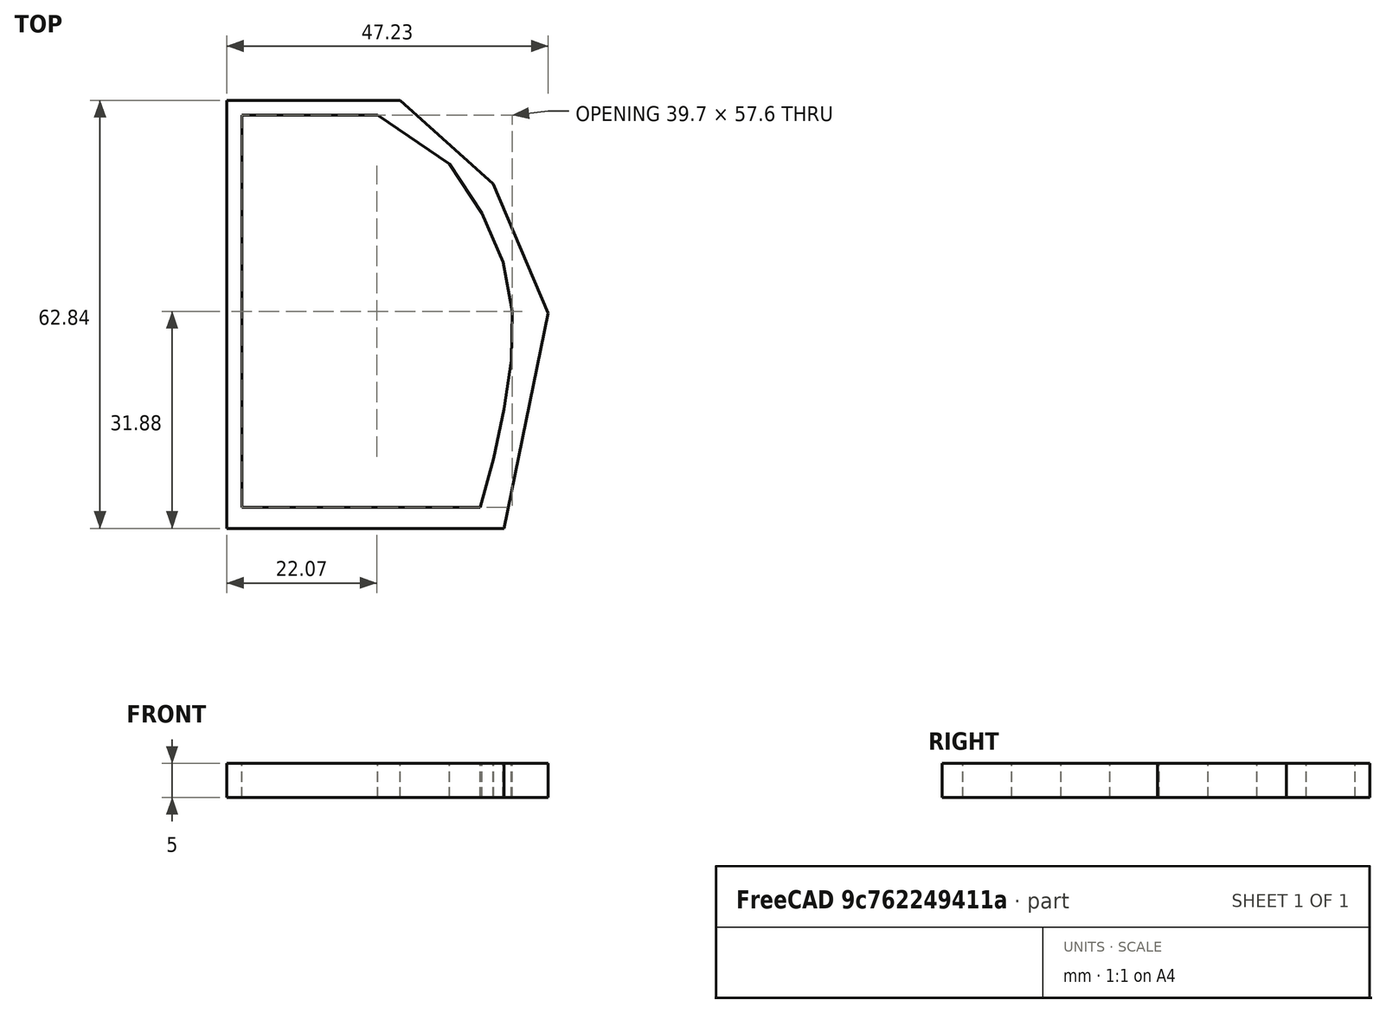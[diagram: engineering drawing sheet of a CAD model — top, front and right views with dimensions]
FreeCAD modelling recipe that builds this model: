
FCSTD DOCUMENT  (FreeCAD 0.19R24291 (Git))
Label: test-fob-profile
License: All rights reserved
LicenseURL: http://en.wikipedia.org/wiki/All_rights_reserved
objects: Sketcher::SketchObject×1, PartDesign::Pad×1, PartDesign::Body×1
note: 4 computed .brp shape members not serialized (recipe doc carries the construction recipe); baked Part::Feature solids carry a one-line shape summary decoded from their .brp

FEATURE [Sketcher::SketchObject] Sketch
  FullyConstrained = false
  MapMode = 5
  Support = -> [XY_Plane]
  sketch-geometry (17):
    g0: LineSegment StartX=0 StartY=0 StartZ=0 EndX=35 EndY=0 EndZ=0
    g1: LineSegment StartX=35 StartY=0 StartZ=0 EndX=37 EndY=7.2 EndZ=0
    g2: LineSegment StartX=37 StartY=7.2 StartZ=0 EndX=38.5 EndY=14.4 EndZ=0
    g3: LineSegment StartX=38.5 StartY=14.4 StartZ=0 EndX=39.6 EndY=21.6 EndZ=0
    g4: LineSegment StartX=39.6 StartY=21.6 StartZ=0 EndX=39.7 EndY=28.8 EndZ=0
    g5: LineSegment StartX=39.7 StartY=28.8 StartZ=0 EndX=38.4 EndY=36 EndZ=0
    g6: LineSegment StartX=38.4 StartY=36 StartZ=0 EndX=35.3 EndY=43.2 EndZ=0
    g7: LineSegment StartX=35.3 StartY=43.2 StartZ=0 EndX=30.5 EndY=50.4 EndZ=0
    g8: LineSegment StartX=30.5 StartY=50.4 StartZ=0 EndX=20 EndY=57.6 EndZ=0
    g9: LineSegment StartX=20 StartY=57.6 StartZ=0 EndX=0 EndY=57.6 EndZ=0
    g10: LineSegment StartX=0 StartY=57.6 StartZ=0 EndX=0 EndY=0 EndZ=0
    g11: LineSegment StartX=-2.21516 StartY=59.7598 StartZ=0 EndX=-2.21516 EndY=-3.07541 EndZ=0
    g12: LineSegment StartX=-2.21516 StartY=-3.07541 StartZ=0 EndX=38.4894 EndY=-3.07541 EndZ=0
    g13: LineSegment StartX=38.4894 StartY=-3.07541 StartZ=0 EndX=45.01 EndY=28.5398 EndZ=0
    g14: LineSegment StartX=45.01 StartY=28.5398 StartZ=0 EndX=36.9087 EndY=47.5089 EndZ=0
    g15: LineSegment StartX=36.9087 StartY=47.5089 StartZ=0 EndX=23.2746 EndY=59.7598 EndZ=0
    g16: LineSegment StartX=23.2746 StartY=59.7598 StartZ=0 EndX=-2.21516 EndY=59.7598 EndZ=0
  constraints (41):
    c: Coincident(g-1,g0)
    c: PointOnObject(g0,g-1)
    c: Coincident(g0,g1)
    c: Coincident(g1,g2)
    c: Coincident(g2,g3)
    c: Coincident(g3,g4)
    c: Coincident(g4,g5)
    c: Coincident(g5,g6)
    c: Coincident(g6,g7)
    c: Coincident(g7,g8)
    c: Coincident(g8,g9)
    c: PointOnObject(g9,g-2)
    c: Horizontal(g9)
    c: Coincident(g9,g10)
    c: Coincident(g10,g0)
    c: DistanceX(g0,g1) = 37
    c: DistanceX(g0,g2) = 38.5
    c: DistanceX(g0,g3) = 39.6
    c: DistanceX(g0,g4) = 39.7
    c: DistanceX(g0,g5) = 38.4
    c: DistanceX(g0,g6) = 35.3
    c: DistanceX(g0,g7) = 30.5
    c: DistanceX(g0,g8) = 20
    c: DistanceX(g0,g0) = 35
    c: DistanceY(g7,g8) = 7.2
    c: DistanceY(g6,g7) = 7.2
    c: DistanceY(g5,g6) = 7.2
    c: DistanceY(g4,g5) = 7.2
    c: DistanceY(g3,g4) = 7.2
    c: DistanceY(g2,g3) = 7.2
    c: DistanceY(g1,g2) = 7.2
    c: DistanceY(g0,g1) = 7.2
    c: Vertical(g11)
    c: Coincident(g11,g12)
    c: Horizontal(g12)
    c: Coincident(g12,g13)
    c: Coincident(g13,g14)
    c: Coincident(g14,g15)
    c: Coincident(g15,g16)
    c: Coincident(g16,g11)
    c: Horizontal(g16)
FEATURE [PartDesign::Pad] Pad
  Direction = (1,1,1)
  Length = 5
  Length2 = 100
  Profile = -> Sketch
  Type = 0
FEATURE [PartDesign::Body] Body
  Group = -> [Sketch,Pad]
  Origin = -> Origin
  Tip = -> Pad
